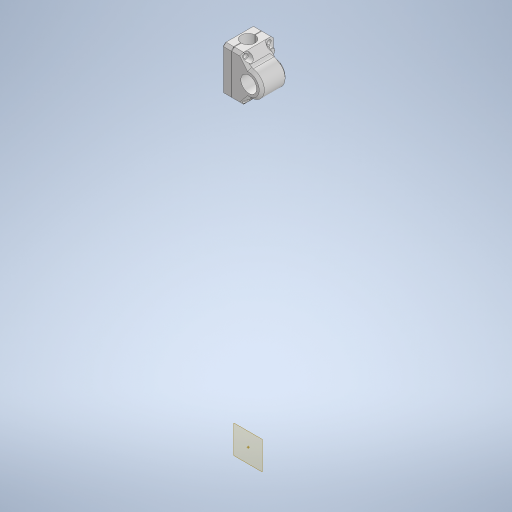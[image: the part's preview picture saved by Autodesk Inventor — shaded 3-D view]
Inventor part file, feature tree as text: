
AUTODESK INVENTOR PART (.ipt)
format: ipt  version: 2024.1 (Build 281209000, 209)  size: 630,784 bytes
history: native  units: mm
features: extrude x11, sketch x11, chamfer x9, other x7, projected_geometry x3, plane x2, fillet x2, reference x2
ambient origin geometry x8: Origin, YZ Plane, XZ Plane, XY Plane, X Axis, Y Axis, Z Axis, Center Point
bodies: Body1 (feature_tree), Body2 (feature_tree), Body3 (feature_tree)
feature tree (47):
  other  "clamp-top"
  plane  "Work Plane1"
  plane  "Work Plane2"
  extrude  "Extrusion1"  Depth=7.5mm
  extrude  "Extrusion2"  Depth=35.0mm TaperAngle=0.0deg
  extrude  "Extrusion3"  Depth=12.3mm
  chamfer  "Chamfer2"  Distance=30.0mm
  extrude  "Extrusion4"  Depth=4.7mm
  chamfer  "Chamfer3"  Distance=2.0mm Angle=45.0deg
  extrude  "Extrusion5"  Depth=3.2mm
  chamfer  "Chamfer4"  Distance=6.0mm
  extrude  "Extrusion7"  Depth=4.0mm
  extrude  "Extrusion6"  Depth=4.0mm
  fillet  "Fillet1"  Radius=3.5mm
  chamfer  "Chamfer9"  [1 undecoded]
  chamfer  "Chamfer10"  Distance=5.45mm
  extrude  "Extrusion8"  Depth=10.0mm TaperAngle=0.0deg
  chamfer  "Chamfer11"  Distance=2.0mm Angle=45.0deg
  chamfer  "Chamfer12"  Distance=6.0mm
  extrude  "Extrusion9"  Depth=4.0mm
  extrude  "Extrusion10"  Depth=4.0mm TaperAngle=45.0deg
  extrude  "Extrusion11"  Depth=4.0mm
  chamfer  "Chamfer13"  Distance=3.0mm
  fillet  "Fillet2"  Radius=0.3mm
  chamfer  "Chamfer1"  Distance=1.0mm
  other  "Work Point1"
  sketch  "Sketch2"  dims[d0=7.5mm d1=7.5mm]
  reference  "Reference1"
  sketch  "Sketch3"  dims[d2=2.0mm d3=35.0mm d4=0.0mm]
  sketch  "Sketch4"  dims[d5=0.25mm d6=12.3mm]
  projected_geometry  "Projected Loop1"
  projected_geometry  "Projected Loop2"
  projected_geometry  "Projected Loop3"
  sketch  "Sketch5"  dims[d7=6.0mm]
  sketch  "Sketch6"  dims[d9=4.0mm d10=30.0mm d11=0.0mm]
  sketch  "Sketch7"  dims[d12=0.0mm d13=0.0mm d14=4.7mm]
  other  "screw-cap"
  sketch  "Sketch8"  dims[d15=4.7mm d16=2.0mm d17=2.0mm d18=45.0deg]
  sketch  "Sketch9"  dims[d19=3.0mm d20=2.0mm d21=45.0deg d22=3.2mm]
  reference  "Reference2"
  other  "clamp-base"
  sketch  "Sketch10"  dims[d23=3.0mm]
  sketch  "Sketch11"  dims[d24=3.0mm]
  sketch  "Sketch12"  dims[d25=6.0mm d26=6.0mm d27=3.0mm d28=3.0mm d29=3.5mm d31=0.0mm d32=0.0mm d33=5.45mm d34=10.0mm d35=0.0mm d36=2.0mm d37=2.0mm d38=45.0deg d39=6.0mm d40=3.5mm d41=2.0mm d42=2.0mm d43=45.0deg d47=5.35mm d48=3.0mm d49=0.0mm d50=0.3mm d51=1.0mm d52=0.0mm d62=2.0mm d63=2.0mm d64=45.0deg d65=1.2mm d66=2.0mm d67=45.0deg d68=0.5mm d69=8.0mm d70=1.0mm d71=0.0mm d72=2.0mm d73=2.0mm d74=45.0deg d75=2.0mm d76=2.0mm d77=45.0deg d78=0.0mm d79=0.0mm d80=4.92mm d81=10.0mm d82=0.0mm d83=35.0mm d84=17.5mm d85=0.0mm d86=0.0mm d87=2.0mm d88=2.0mm d89=45.0deg d90=4.0mm]
  other  "<userpath>\Documents\0004-CAD\3D-cad-main\bike-rack\bike-rack-assembly.iam"
  other  "bike-rack-assembly.iam"
  other  "bike-rack:1"
note: 1 required parameter value undecoded (feature->parameter linkage not recoverable at this tier; creation-order binding heuristic only, values carry confidence <= 0.55)
